# Revit family: LC Duplex 12 fibers
name_source: partatom
category: Installations électriques
units: mm (PartAtom-declared; Revit-internal decimal feet)

## family parameters
Basée sur le plan de construction = Non
Conserver l'orientation des annotations = Non
Cote de connecteur circulaire = Utiliser le diamètre
Couper avec des vides une fois chargée = Non
Partagée = Non
Point de calcul de pièce = Non
Toujours verticalement = Oui
Type d'élément = Normal

## types (4) — shared parameters
Color = IDS_NOIR
Depth = 38.4 mm  [stored 0.125984 ft]
E-catalogue link = https://www.legrand.fr
ETIM class = EC001130
Function = Patch panels with optical connector Legrand
Height = 23 mm  [stored 0.0754593 ft]
Height of the connectors = 10 mm  [stored 0.0328084 ft]
IK = IK04
IP = IP20
Number of connectors = 12
Opening height = 6.5 mm
Opening width = 6 mm  [stored 0.019685 ft]
Operating temperature = -10°C à 60°C
RAL Number = 9017
Storage temperature = -10°C à 60°C
Width (mm) = 108.8 mm  [stored 0.356955 ft]
Width of the connectors = 13.5 mm  [stored 0.0442913 ft]
zero-valued in all types: Elévation par défaut

## per-type parameters (varying)
| type | BIM wording | Colour of the connectors | EAN | Fiber optic type | Legrand part number | Type of connector external | Type of connector interior |
| LC Duplex block 12 fibers single mode | LC Duplex block 12 fibers single mode | IDS_BLEU | 3414970961730 | Single mode | 032114 | LC_DUPLEX | LC_DUPLEX |
| LC APC Duplex block 12 fibers single mode | LC APC Duplex block 12 fibers single mode | IDS_CYAN | 3414970961778 | Single mode | 032116 | LC-DUPLEX | LC-DUPLEX |
| LC Duplex block 12 fibers multimode | LC Duplex block 12 fibers multimode | IDS_JAUNE | 3414970961877 | Multimode | 032124 | LC_DUPLEX | LC_DUPLEX |
| LC Duplex block(AQUA)_POUR_12_FIBRES_MULTIMODE | LC Duplex block 12 fibers multimode | IDS_CYAN | 3414971400313 | Multimode | 032137 | LC_DUPLEX | LC_DUPLEX |

note: [stored X ft] marks values corroborated as IEEE doubles in the binary element streams (Revit-internal decimal feet)
